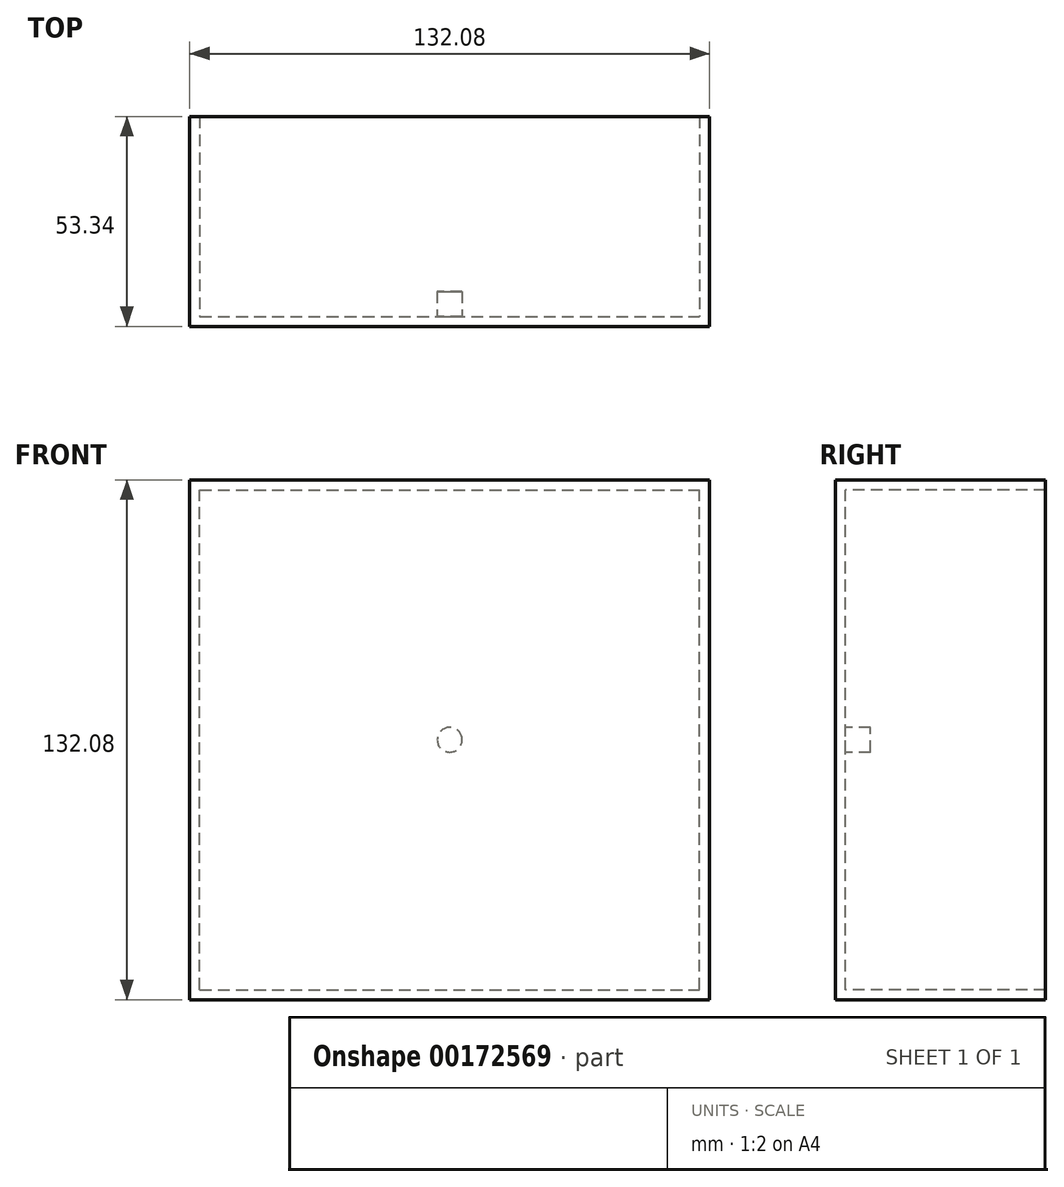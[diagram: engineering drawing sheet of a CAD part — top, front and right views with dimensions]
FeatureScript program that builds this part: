
annotation { "Feature Type Name" : "Feature", "Feature Type Description" : "" }
export const myFeature = defineFeature(function(context is Context, id is Id, definition is map)
    precondition{}
    {
        {
            var Q0;
            Q0=qCreatedBy(makeId("Front.planeOp"),FACE);
            var sketch = newSketch(context, id + "F0", { "sketchPlane" : qUnion([Q0])});
            skLineSegment(sketch, "E0.bottom", {"start": v(-63.5, -63.5) * mm, "end": v(63.5, -63.5) * mm});
            skLineSegment(sketch, "E0.top", {"start": v(-63.5, 63.5) * mm, "end": v(63.5, 63.5) * mm});
            skLineSegment(sketch, "E0.left", {"start": v(-63.5, -63.5) * mm, "end": v(-63.5, 63.5) * mm});
            skLineSegment(sketch, "E0.right", {"start": v(63.5, -63.5) * mm, "end": v(63.5, 63.5) * mm});
            skPoint(sketch, "E0.middle", {"position": v(0, 0) * mm});
            skSolve(sketch);
        }
        {
            var Q0;
            Q0=makeQuery(id+"F0.imprint","IMPRINT",FACE,{"disambiguationData":[TD([[makeQuery(id+"F0.imprint","IMPRINT",EDGE,{"derivedFrom":sQuery(id+"F0.wireOp",EDGE,"E0.bottom")}),1.0]])]});
            extrude(context, id + "F1", {"entities" : qUnion([Q0]), "oppositeDirection" : true, "depth" : 50.8 * mm});
        }
        {
            var Q0;
            Q0=makeQuery(id+"F1.opExtrude","CAP_FACE",FACE,{"disambiguationData":[OSD([sQuery(id+"F0.wireOp",EDGE,"E0.bottom"),sQuery(id+"F0.wireOp",EDGE,"E0.top"),sQuery(id+"F0.wireOp",EDGE,"E0.left"),sQuery(id+"F0.wireOp",EDGE,"E0.right")])],"isStart":true});
            var sketch = newSketch(context, id + "F2", { "sketchPlane" : qUnion([Q0])});
            skCircle(sketch, "E1", {"center": v(0, 0) * mm, "radius": 3.18 * mm});
            skSolve(sketch);
        }
        {
            var Q0;
            Q0=makeQuery(id+"F2.imprint","IMPRINT",FACE,{"disambiguationData":[TD([[makeQuery(id+"F2.imprint","IMPRINT",EDGE,{"derivedFrom":sQuery(id+"F2.wireOp",EDGE,"E1")}),1.0]])]});
            extrude(context, id + "F3", {"entities" : qUnion([Q0]), "oppositeDirection" : true, "depth" : 6.35 * mm});
        }
        {
            var Q0;
            Q0=makeQuery(id+"F1.opExtrude","CAP_FACE",FACE,{"disambiguationData":[OSD([sQuery(id+"F0.wireOp",EDGE,"E0.bottom"),sQuery(id+"F0.wireOp",EDGE,"E0.top"),sQuery(id+"F0.wireOp",EDGE,"E0.left"),sQuery(id+"F0.wireOp",EDGE,"E0.right")])],"isStart":false});
            shell(context, id + "F4", {"entities" : qUnion([Q0]), "thickness" : 2.54 * mm, "oppositeDirection" : true});
        }
    });
